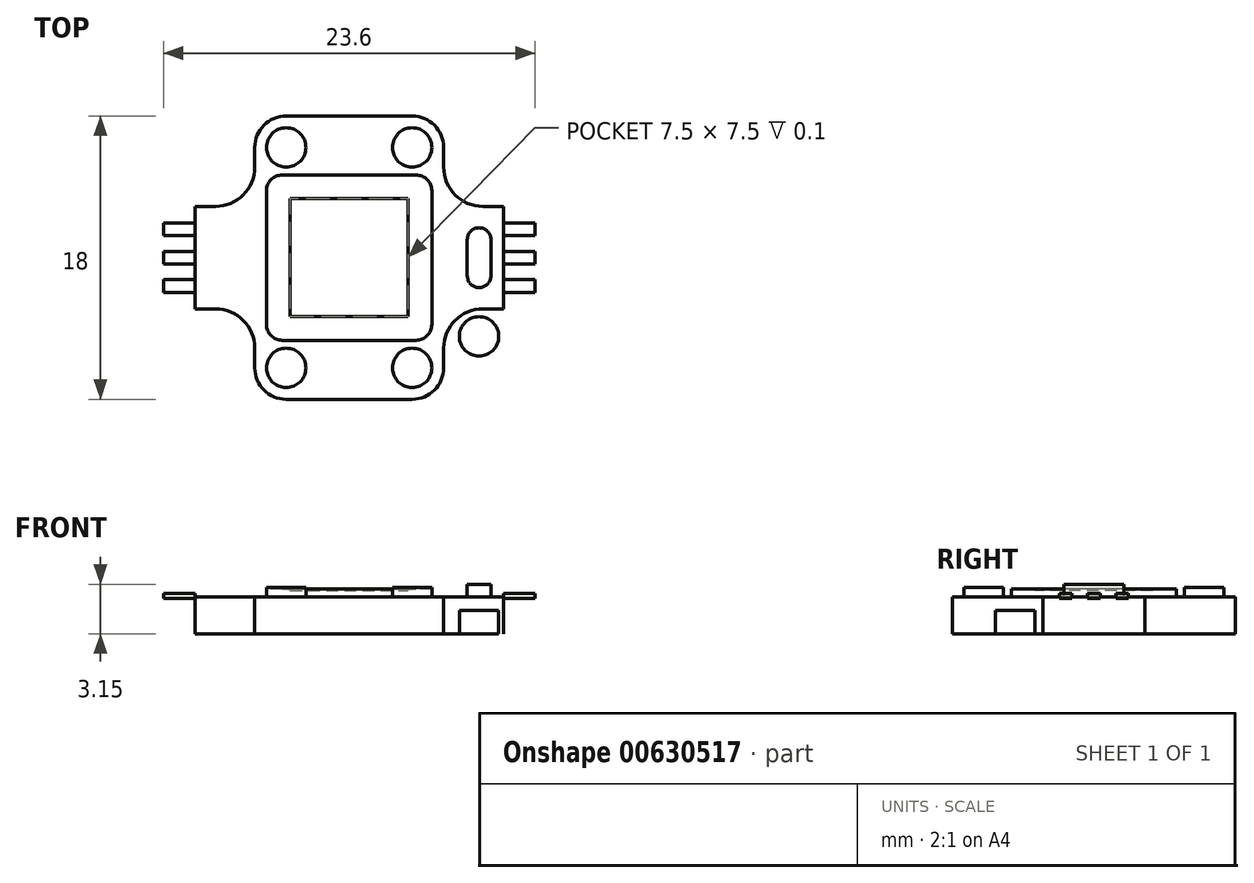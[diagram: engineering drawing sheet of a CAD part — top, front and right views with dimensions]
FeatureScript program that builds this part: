
annotation { "Feature Type Name" : "Feature", "Feature Type Description" : "" }
export const myFeature = defineFeature(function(context is Context, id is Id, definition is map)
    precondition{}
    {
        {
            var Q0;
            Q0=qCreatedBy(makeId("Top.planeOp"),FACE);
            var sketch = newSketch(context, id + "F0", { "sketchPlane" : qUnion([Q0])});
            skLineSegment(sketch, "E0", {"start": v(-10, 7.05) * mm, "end": v(-10, -7.05) * mm});
            skLineSegment(sketch, "E1", {"start": v(-7.05, -10) * mm, "end": v(7.05, -10) * mm});
            skLineSegment(sketch, "E2", {"start": v(10, 7.05) * mm, "end": v(10, -7.05) * mm});
            skLineSegment(sketch, "E3", {"start": v(-7.05, 10) * mm, "end": v(7.05, 10) * mm});
            skArc(sketch, "E4", {"start": v(-7.05, -10) * mm, "mid": v(-7.73, -7.73) * mm, "end": v(-10, -7.05) * mm});
            skArc(sketch, "E5", {"start": v(-10, 7.05) * mm, "mid": v(-7.73, 7.73) * mm, "end": v(-7.05, 10) * mm});
            skArc(sketch, "E6", {"start": v(10, -7.05) * mm, "mid": v(7.73, -7.73) * mm, "end": v(7.05, -10) * mm});
            skArc(sketch, "E7", {"start": v(7.05, 10) * mm, "mid": v(7.73, 7.73) * mm, "end": v(10, 7.05) * mm});
            skSolve(sketch);
        }
        {
            var Q0;
            Q0=makeQuery(id+"F0.imprint","IMPRINT",FACE,{"disambiguationData":[TD([[makeQuery(id+"F0.imprint","IMPRINT",EDGE,{"derivedFrom":sQuery(id+"F0.wireOp",EDGE,"E0")}),1.0]])]});
            extrude(context, id + "F1", {"entities" : qUnion([Q0]), "depth" : 1.5 * mm, "offsetDistance" : 25 * mm});
        }
        {
            var Q0;
            Q0=makeQuery(id+"F1.opExtrude","CAP_FACE",FACE,{"disambiguationData":[OSD([sQuery(id+"F0.wireOp",EDGE,"E0"),sQuery(id+"F0.wireOp",EDGE,"E1"),sQuery(id+"F0.wireOp",EDGE,"E2"),sQuery(id+"F0.wireOp",EDGE,"E3"),sQuery(id+"F0.wireOp",EDGE,"E4"),sQuery(id+"F0.wireOp",EDGE,"E5"),sQuery(id+"F0.wireOp",EDGE,"E6"),sQuery(id+"F0.wireOp",EDGE,"E7")])],"isStart":false});
            var sketch = newSketch(context, id + "F2", { "sketchPlane" : qUnion([Q0])});
            skLineSegment(sketch, "E8", {"start": v(-6, 5.75) * mm, "end": v(-6, 7) * mm});
            skLineSegment(sketch, "E9", {"start": v(-4, 9) * mm, "end": v(4, 9) * mm});
            skLineSegment(sketch, "E10", {"start": v(6, 7) * mm, "end": v(6, 5.75) * mm});
            skLineSegment(sketch, "E11", {"start": v(-8.5, 3.25) * mm, "end": v(-9.8, 3.25) * mm});
            skLineSegment(sketch, "E12", {"start": v(8.5, 3.25) * mm, "end": v(9.8, 3.25) * mm});
            skPoint(sketch, "E13.visualSharp", {"position": v(-6, 3.25) * mm});
            skArc(sketch, "E13.filletArc", {"start": v(-8.5, 3.25) * mm, "mid": v(-6.73, 3.98) * mm, "end": v(-6, 5.75) * mm});
            skPoint(sketch, "E14.visualSharp", {"position": v(-6, 9) * mm});
            skArc(sketch, "E14.filletArc", {"start": v(-4, 9) * mm, "mid": v(-5.41, 8.41) * mm, "end": v(-6, 7) * mm});
            skPoint(sketch, "E15.visualSharp", {"position": v(6, 9) * mm});
            skArc(sketch, "E15.filletArc", {"start": v(6, 7) * mm, "mid": v(5.41, 8.41) * mm, "end": v(4, 9) * mm});
            skPoint(sketch, "E16.visualSharp", {"position": v(6, 3.25) * mm});
            skLineSegment(sketch, "E17", {"start": v(-10, 0) * mm, "end": v(10, 0) * mm, "construction": true});
            skLineSegment(sketch, "E18.MirrorCS", {"start": v(-8.5, -3.25) * mm, "end": v(-9.8, -3.25) * mm});
            skArc(sketch, "E19.MirrorCS", {"start": v(-8.5, -3.25) * mm, "mid": v(-6.73, -3.98) * mm, "end": v(-6, -5.75) * mm});
            skLineSegment(sketch, "E20.MirrorCS", {"start": v(-6, -5.75) * mm, "end": v(-6, -7) * mm});
            skArc(sketch, "E21.MirrorCS", {"start": v(-4, -9) * mm, "mid": v(-5.41, -8.41) * mm, "end": v(-6, -7) * mm});
            skLineSegment(sketch, "E22.MirrorCS", {"start": v(-4, -9) * mm, "end": v(4, -9) * mm});
            skArc(sketch, "E23.MirrorCS", {"start": v(6, -7) * mm, "mid": v(5.41, -8.41) * mm, "end": v(4, -9) * mm});
            skLineSegment(sketch, "E24.MirrorCS", {"start": v(6, -7) * mm, "end": v(6, -5.75) * mm});
            skLineSegment(sketch, "E25.MirrorCS", {"start": v(8.5, -3.25) * mm, "end": v(9.8, -3.25) * mm});
            skLineSegment(sketch, "E26", {"start": v(-9.8, 3.25) * mm, "end": v(-9.8, -3.25) * mm});
            skPoint(sketch, "E27.orphan", {"position": v(-10, 3.25) * mm});
            skPoint(sketch, "E28.orphan", {"position": v(-10, -3.25) * mm});
            skLineSegment(sketch, "E29", {"start": v(9.8, 3.25) * mm, "end": v(9.8, -3.25) * mm});
            skPoint(sketch, "E30.orphan", {"position": v(10, 3.25) * mm});
            skPoint(sketch, "E31.orphan", {"position": v(10, -3.25) * mm});
            skArc(sketch, "E32.MirrorCS", {"start": v(8.5, 3.25) * mm, "mid": v(6.73, 3.98) * mm, "end": v(6, 5.75) * mm});
            skArc(sketch, "E33.MirrorCS", {"start": v(8.5, -3.25) * mm, "mid": v(6.73, -3.98) * mm, "end": v(6, -5.75) * mm});
            skSolve(sketch);
        }
        {
            var Q0;
            Q0=makeQuery(id+"F2.imprint","IMPRINT",FACE,{"disambiguationData":[TD([[makeQuery(id+"F2.imprint","IMPRINT",EDGE,{"derivedFrom":sQuery(id+"F2.wireOp",EDGE,"E8")}),-1.0]])]});
            extrude(context, id + "F3", {"entities" : qUnion([Q0]), "operationType" : NewBodyOperationType.ADD, "depth" : 1.65 * mm, "offsetDistance" : 25 * mm});
        }
        {
            var Q0;
            Q0=makeQuery(id+"F3.opExtrude","CAP_FACE",FACE,{"disambiguationData":[OSD([sQuery(id+"F0.wireOp",EDGE,"E0"),sQuery(id+"F0.wireOp",EDGE,"E2"),sQuery(id+"F2.wireOp",EDGE,"E8"),sQuery(id+"F2.wireOp",EDGE,"E9"),sQuery(id+"F2.wireOp",EDGE,"E10"),sQuery(id+"F2.wireOp",EDGE,"E12"),sQuery(id+"F2.wireOp",EDGE,"E13.filletArc"),sQuery(id+"F2.wireOp",EDGE,"E14.filletArc"),sQuery(id+"F2.wireOp",EDGE,"E15.filletArc"),sQuery(id+"F2.wireOp",EDGE,"E16.filletArc"),sQuery(id+"F2.wireOp",EDGE,"49ddf0b0-b372-4877-a7fa-4dc4355d94440.MirrorCS"),sQuery(id+"F2.wireOp",EDGE,"E18.MirrorCS"),sQuery(id+"F2.wireOp",EDGE,"E19.MirrorCS"),sQuery(id+"F2.wireOp",EDGE,"E20.MirrorCS"),sQuery(id+"F2.wireOp",EDGE,"E21.MirrorCS"),sQuery(id+"F2.wireOp",EDGE,"E22.MirrorCS"),sQuery(id+"F2.wireOp",EDGE,"E23.MirrorCS"),sQuery(id+"F2.wireOp",EDGE,"E24.MirrorCS"),sQuery(id+"F2.wireOp",EDGE,"0bbfe62d-6cfe-40ae-9e74-ae4129ddde330.MirrorCS"),sQuery(id+"F2.wireOp",EDGE,"E25.MirrorCS")])],"isStart":false});
            var sketch = newSketch(context, id + "F4", { "sketchPlane" : qUnion([Q0])});
            skLineSegment(sketch, "E34.bottom", {"start": v(-4.25, 5.25) * mm, "end": v(4.25, 5.25) * mm});
            skLineSegment(sketch, "E34.top", {"start": v(-4.25, -5.25) * mm, "end": v(4.25, -5.25) * mm});
            skLineSegment(sketch, "E34.left", {"start": v(-5.25, 4.25) * mm, "end": v(-5.25, -4.25) * mm});
            skLineSegment(sketch, "E34.right", {"start": v(5.25, 4.25) * mm, "end": v(5.25, -4.25) * mm});
            skPoint(sketch, "E35.visualSharp", {"position": v(-5.25, 5.25) * mm});
            skArc(sketch, "E35.filletArc", {"start": v(-4.25, 5.25) * mm, "mid": v(-4.96, 4.96) * mm, "end": v(-5.25, 4.25) * mm});
            skPoint(sketch, "E36.visualSharp", {"position": v(5.25, 5.25) * mm});
            skArc(sketch, "E36.filletArc", {"start": v(5.25, 4.25) * mm, "mid": v(4.96, 4.96) * mm, "end": v(4.25, 5.25) * mm});
            skPoint(sketch, "E37.visualSharp", {"position": v(5.25, -5.25) * mm});
            skArc(sketch, "E37.filletArc", {"start": v(4.25, -5.25) * mm, "mid": v(4.96, -4.96) * mm, "end": v(5.25, -4.25) * mm});
            skPoint(sketch, "E38.visualSharp", {"position": v(-5.25, -5.25) * mm});
            skArc(sketch, "E38.filletArc", {"start": v(-5.25, -4.25) * mm, "mid": v(-4.96, -4.96) * mm, "end": v(-4.25, -5.25) * mm});
            skSolve(sketch);
        }
        {
            var Q0;
            Q0 = qSketchRegion(id + "F4", true);
            extrude(context, id + "F5", {"entities" : qUnion([Q0]), "operationType" : NewBodyOperationType.REMOVE, "oppositeDirection" : true, "depth" : 0.3 * mm, "offsetDistance" : 25 * mm});
        }
        {
            var Q0;
            Q0=makeQuery(id+"F3.opExtrude","CAP_FACE",FACE,{"disambiguationData":[OSD([sQuery(id+"F0.wireOp",EDGE,"E0"),sQuery(id+"F0.wireOp",EDGE,"E2"),sQuery(id+"F2.wireOp",EDGE,"E8"),sQuery(id+"F2.wireOp",EDGE,"E9"),sQuery(id+"F2.wireOp",EDGE,"E10"),sQuery(id+"F2.wireOp",EDGE,"E12"),sQuery(id+"F2.wireOp",EDGE,"E13.filletArc"),sQuery(id+"F2.wireOp",EDGE,"E14.filletArc"),sQuery(id+"F2.wireOp",EDGE,"E15.filletArc"),sQuery(id+"F2.wireOp",EDGE,"E16.filletArc"),sQuery(id+"F2.wireOp",EDGE,"49ddf0b0-b372-4877-a7fa-4dc4355d94440.MirrorCS"),sQuery(id+"F2.wireOp",EDGE,"E18.MirrorCS"),sQuery(id+"F2.wireOp",EDGE,"E19.MirrorCS"),sQuery(id+"F2.wireOp",EDGE,"E20.MirrorCS"),sQuery(id+"F2.wireOp",EDGE,"E21.MirrorCS"),sQuery(id+"F2.wireOp",EDGE,"E22.MirrorCS"),sQuery(id+"F2.wireOp",EDGE,"E23.MirrorCS"),sQuery(id+"F2.wireOp",EDGE,"E24.MirrorCS"),sQuery(id+"F2.wireOp",EDGE,"0bbfe62d-6cfe-40ae-9e74-ae4129ddde330.MirrorCS"),sQuery(id+"F2.wireOp",EDGE,"E25.MirrorCS")])],"isStart":false});
            var sketch = newSketch(context, id + "F6", { "sketchPlane" : qUnion([Q0])});
            skCircle(sketch, "E39", {"center": v(-4, 7) * mm, "radius": 1.25 * mm});
            skCircle(sketch, "E40", {"center": v(4, 7) * mm, "radius": 1.25 * mm});
            skCircle(sketch, "E41.MirrorC", {"center": v(-4, -7) * mm, "radius": 1.25 * mm});
            skCircle(sketch, "E42.MirrorC", {"center": v(4, -7) * mm, "radius": 1.25 * mm});
            skSolve(sketch);
        }
        {
            var Q0;
            Q0 = qSketchRegion(id + "F6", true);
            extrude(context, id + "F7", {"entities" : qUnion([Q0]), "operationType" : NewBodyOperationType.REMOVE, "oppositeDirection" : true, "depth" : 0.2 * mm, "offsetDistance" : 25 * mm});
        }
        {
            var Q0;
            Q0=makeQuery(id+"F3.opExtrude","SWEPT_FACE",FACE,{"disambiguationData":[OSD([sQuery(id+"F2.wireOp",EDGE,"E26")])]});
            var sketch = newSketch(context, id + "F8", { "sketchPlane" : qUnion([Q0])});
            skLineSegment(sketch, "E43.bottom", {"start": v(-0.4, 2.57) * mm, "end": v(0.4, 2.57) * mm});
            skLineSegment(sketch, "E43.top", {"start": v(-0.4, 2.27) * mm, "end": v(0.4, 2.27) * mm});
            skLineSegment(sketch, "E43.left", {"start": v(-0.4, 2.57) * mm, "end": v(-0.4, 2.27) * mm});
            skLineSegment(sketch, "E43.right", {"start": v(0.4, 2.57) * mm, "end": v(0.4, 2.27) * mm});
            skLineSegment(sketch, "E44", {"start": v(-3.25, 2.32) * mm, "end": v(3.25, 2.32) * mm, "construction": true});
            skLineSegment(sketch, "E45.bottom", {"start": v(1.4, 2.57) * mm, "end": v(2.2, 2.57) * mm});
            skLineSegment(sketch, "E45.top", {"start": v(1.4, 2.27) * mm, "end": v(2.2, 2.27) * mm});
            skLineSegment(sketch, "E45.left", {"start": v(1.4, 2.57) * mm, "end": v(1.4, 2.27) * mm});
            skLineSegment(sketch, "E45.right", {"start": v(2.2, 2.57) * mm, "end": v(2.2, 2.27) * mm});
            skLineSegment(sketch, "E46", {"start": v(0, 3.15) * mm, "end": v(0, 1.5) * mm, "construction": true});
            skLineSegment(sketch, "E47", {"start": v(0, 1.5) * mm, "end": v(0, 3.15) * mm, "construction": true});
            skLineSegment(sketch, "E48.MirrorCS", {"start": v(-1.4, 2.57) * mm, "end": v(-1.4, 2.27) * mm});
            skLineSegment(sketch, "E49.MirrorCS", {"start": v(-1.4, 2.57) * mm, "end": v(-2.2, 2.57) * mm});
            skLineSegment(sketch, "E50.MirrorCS", {"start": v(-1.4, 2.27) * mm, "end": v(-2.2, 2.27) * mm});
            skLineSegment(sketch, "E51.MirrorCS", {"start": v(-2.2, 2.57) * mm, "end": v(-2.2, 2.27) * mm});
            skSolve(sketch);
        }
        {
            var Q0;
            Q0 = qSketchRegion(id + "F8", true);
            extrude(context, id + "F9", {"entities" : qUnion([Q0]), "depth" : 2 * mm, "offsetDistance" : 25 * mm});
        }
        {
            var Q0;
            Q0=makeQuery(id+"F9.opExtrude","SWEPT_BODY",BODY,{"disambiguationData":[OSD([sQuery(id+"F8.wireOp",EDGE,"E48.MirrorCS"),sQuery(id+"F8.wireOp",EDGE,"E49.MirrorCS"),sQuery(id+"F8.wireOp",EDGE,"E50.MirrorCS"),sQuery(id+"F8.wireOp",EDGE,"E51.MirrorCS")])]});
            var Q1;
            Q1=makeQuery(id+"F9.opExtrude","SWEPT_BODY",BODY,{"disambiguationData":[OSD([sQuery(id+"F8.wireOp",EDGE,"E43.bottom"),sQuery(id+"F8.wireOp",EDGE,"E43.top"),sQuery(id+"F8.wireOp",EDGE,"E43.left"),sQuery(id+"F8.wireOp",EDGE,"E43.right")])]});
            var Q2;
            Q2=makeQuery(id+"F9.opExtrude","SWEPT_BODY",BODY,{"disambiguationData":[OSD([sQuery(id+"F8.wireOp",EDGE,"E45.bottom"),sQuery(id+"F8.wireOp",EDGE,"E45.top"),sQuery(id+"F8.wireOp",EDGE,"E45.left"),sQuery(id+"F8.wireOp",EDGE,"E45.right")])]});
            var Q3;
            Q3=qCreatedBy(makeId("Right.planeOp"),FACE);
            mirror(context, id + "F10", {"operationType" : NewBodyOperationType.ADD, "entities" : qUnion([Q0, Q1, Q2]), "mirrorPlane" : qUnion([Q3])});
        }
        {
            var Q0;
            Q0=makeQuery(id+"F1.opExtrude","CAP_FACE",FACE,{"disambiguationData":[OSD([sQuery(id+"F0.wireOp",EDGE,"E0"),sQuery(id+"F0.wireOp",EDGE,"E1"),sQuery(id+"F0.wireOp",EDGE,"E2"),sQuery(id+"F0.wireOp",EDGE,"E3"),sQuery(id+"F0.wireOp",EDGE,"E4"),sQuery(id+"F0.wireOp",EDGE,"E5"),sQuery(id+"F0.wireOp",EDGE,"E6"),sQuery(id+"F0.wireOp",EDGE,"E7")])],"isStart":false});
            var sketch = newSketch(context, id + "F11", { "sketchPlane" : qUnion([Q0])});
            skCircle(sketch, "E52", {"center": v(-8.25, -5) * mm, "radius": 1.25 * mm});
            skCircle(sketch, "E53.MirrorC", {"center": v(8.25, -5) * mm, "radius": 1.25 * mm});
            skSolve(sketch);
        }
        {
            var Q0;
            Q0=makeQuery(id+"F11.imprint","IMPRINT",FACE,{"disambiguationData":[TD([[makeQuery(id+"F11.imprint","IMPRINT",EDGE,{"derivedFrom":sQuery(id+"F11.wireOp",EDGE,"E52")}),1.0]])]});
            var Q1;
            Q1=makeQuery(id+"F11.imprint","IMPRINT",FACE,{"disambiguationData":[TD([[makeQuery(id+"F11.imprint","IMPRINT",EDGE,{"derivedFrom":sQuery(id+"F11.wireOp",EDGE,"E53.MirrorC")}),-1.0]])]});
            extrude(context, id + "F12", {"entities" : qUnion([Q0, Q1]), "operationType" : NewBodyOperationType.REMOVE, "endBound" : BoundingType.UP_TO_NEXT, "oppositeDirection" : true, "depth" : 25 * mm, "offsetDistance" : 25 * mm});
        }
        {
            var Q0;
            Q0=makeQuery(id+"F3.opExtrude","CAP_FACE",FACE,{"disambiguationData":[OSD([sQuery(id+"F2.wireOp",EDGE,"E8"),sQuery(id+"F2.wireOp",EDGE,"E9"),sQuery(id+"F2.wireOp",EDGE,"E10"),sQuery(id+"F2.wireOp",EDGE,"E11"),sQuery(id+"F2.wireOp",EDGE,"E12"),sQuery(id+"F2.wireOp",EDGE,"E13.filletArc"),sQuery(id+"F2.wireOp",EDGE,"E14.filletArc"),sQuery(id+"F2.wireOp",EDGE,"E15.filletArc"),sQuery(id+"F2.wireOp",EDGE,"E16.filletArc"),sQuery(id+"F2.wireOp",EDGE,"E18.MirrorCS"),sQuery(id+"F2.wireOp",EDGE,"E19.MirrorCS"),sQuery(id+"F2.wireOp",EDGE,"E20.MirrorCS"),sQuery(id+"F2.wireOp",EDGE,"E21.MirrorCS"),sQuery(id+"F2.wireOp",EDGE,"E22.MirrorCS"),sQuery(id+"F2.wireOp",EDGE,"E23.MirrorCS"),sQuery(id+"F2.wireOp",EDGE,"E24.MirrorCS"),sQuery(id+"F2.wireOp",EDGE,"0bbfe62d-6cfe-40ae-9e74-ae4129ddde330.MirrorCS"),sQuery(id+"F2.wireOp",EDGE,"E25.MirrorCS"),sQuery(id+"F2.wireOp",EDGE,"E26"),sQuery(id+"F2.wireOp",EDGE,"E29")])],"isStart":false});
            var sketch = newSketch(context, id + "F13", { "sketchPlane" : qUnion([Q0])});
            skLineSegment(sketch, "E54", {"start": v(-9, 1.15) * mm, "end": v(-9, -1.15) * mm});
            skLineSegment(sketch, "E55", {"start": v(-7.5, 1.15) * mm, "end": v(-7.5, -1.15) * mm});
            skArc(sketch, "E56", {"start": v(-7.5, 1.15) * mm, "mid": v(-8.25, 1.9) * mm, "end": v(-9, 1.15) * mm});
            skArc(sketch, "E57", {"start": v(-9, -1.15) * mm, "mid": v(-8.25, -1.9) * mm, "end": v(-7.5, -1.15) * mm});
            skArc(sketch, "E58.MirrorCS", {"start": v(9, -1.15) * mm, "mid": v(8.25, -1.9) * mm, "end": v(7.5, -1.15) * mm});
            skLineSegment(sketch, "E59.MirrorCS", {"start": v(7.5, 1.15) * mm, "end": v(7.5, -1.15) * mm});
            skArc(sketch, "E60.MirrorCS", {"start": v(7.5, 1.15) * mm, "mid": v(8.25, 1.9) * mm, "end": v(9, 1.15) * mm});
            skLineSegment(sketch, "E61.MirrorCS", {"start": v(9, 1.15) * mm, "end": v(9, -1.15) * mm});
            skSolve(sketch);
        }
        {
            var Q0;
            Q0=makeQuery(id+"F13.imprint","IMPRINT",FACE,{"disambiguationData":[TD([[makeQuery(id+"F13.imprint","IMPRINT",EDGE,{"derivedFrom":sQuery(id+"F13.wireOp",EDGE,"E54")}),1.0]])]});
            var Q1;
            Q1=makeQuery(id+"F13.imprint","IMPRINT",FACE,{"disambiguationData":[TD([[makeQuery(id+"F13.imprint","IMPRINT",EDGE,{"derivedFrom":sQuery(id+"F13.wireOp",EDGE,"E58.MirrorCS")}),-1.0]])]});
            extrude(context, id + "F14", {"entities" : qUnion([Q0, Q1]), "operationType" : NewBodyOperationType.REMOVE, "oppositeDirection" : true, "depth" : .8 * mm, "offsetDistance" : 25 * mm});
        }
        {
            var Q0;
            Q0=makeQuery(id+"F5.boolean.opBoolean","COPY",FACE,{"derivedFrom":makeQuery(id+"F5.opExtrude","CAP_FACE",FACE,{"disambiguationData":[OSD([sQuery(id+"F4.wireOp",EDGE,"E34.bottom"),sQuery(id+"F4.wireOp",EDGE,"E34.top"),sQuery(id+"F4.wireOp",EDGE,"E34.left"),sQuery(id+"F4.wireOp",EDGE,"E34.right"),sQuery(id+"F4.wireOp",EDGE,"E35.filletArc"),sQuery(id+"F4.wireOp",EDGE,"E36.filletArc"),sQuery(id+"F4.wireOp",EDGE,"E37.filletArc"),sQuery(id+"F4.wireOp",EDGE,"E38.filletArc")])],"isStart":false})});
            var sketch = newSketch(context, id + "F15", { "sketchPlane" : qUnion([Q0])});
            skLineSegment(sketch, "E62.bottom", {"start": v(-3.75, 3.75) * mm, "end": v(3.75, 3.75) * mm});
            skLineSegment(sketch, "E62.top", {"start": v(-3.75, -3.75) * mm, "end": v(3.75, -3.75) * mm});
            skLineSegment(sketch, "E62.left", {"start": v(-3.75, 3.75) * mm, "end": v(-3.75, -3.75) * mm});
            skLineSegment(sketch, "E62.right", {"start": v(3.75, 3.75) * mm, "end": v(3.75, -3.75) * mm});
            skLineSegment(sketch, "E63", {"start": v(-3.75, 3.75) * mm, "end": v(3.75, -3.75) * mm, "construction": true});
            skSolve(sketch);
        }
        {
            var Q0;
            Q0=makeQuery(id+"F15.imprint","IMPRINT",FACE,{"disambiguationData":[TD([[makeQuery(id+"F15.imprint","IMPRINT",EDGE,{"derivedFrom":sQuery(id+"F15.wireOp",EDGE,"E62.bottom")}),-1.0]])]});
            extrude(context, id + "F16", {"entities" : qUnion([Q0]), "operationType" : NewBodyOperationType.REMOVE, "oppositeDirection" : true, "depth" : .1 * mm, "offsetDistance" : 25 * mm});
        }
    });
